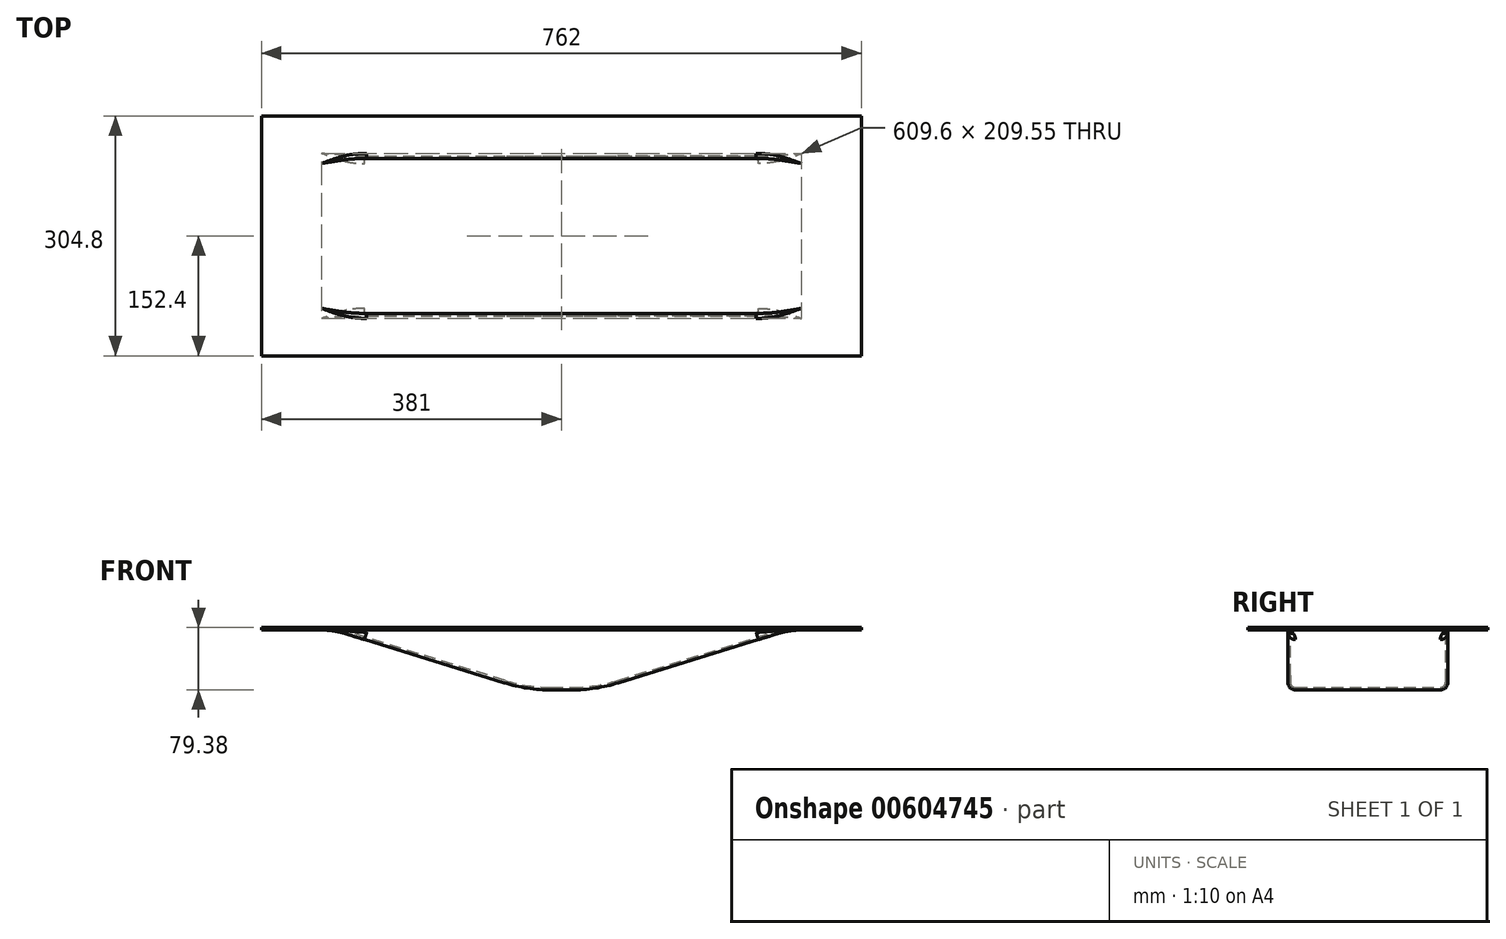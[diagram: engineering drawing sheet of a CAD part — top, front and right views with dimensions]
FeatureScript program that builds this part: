
annotation { "Feature Type Name" : "Feature", "Feature Type Description" : "" }
export const myFeature = defineFeature(function(context is Context, id is Id, definition is map)
    precondition{}
    {
        {
            var Q0;
            Q0=qCreatedBy(makeId("Top.planeOp"),FACE);
            var sketch = newSketch(context, id + "F0", { "sketchPlane" : qUnion([Q0])});
            skLineSegment(sketch, "E0.bottom", {"start": v(-381, 152.4) * mm, "end": v(381, 152.4) * mm});
            skLineSegment(sketch, "E0.top", {"start": v(-381, -152.4) * mm, "end": v(381, -152.4) * mm});
            skLineSegment(sketch, "E0.left", {"start": v(-381, 152.4) * mm, "end": v(-381, -152.4) * mm});
            skLineSegment(sketch, "E0.right", {"start": v(381, 152.4) * mm, "end": v(381, -152.4) * mm});
            skLineSegment(sketch, "E1.bottom", {"start": v(-304.8, 101.6) * mm, "end": v(304.8, 101.6) * mm});
            skLineSegment(sketch, "E1.top", {"start": v(-304.8, -101.6) * mm, "end": v(304.8, -101.6) * mm});
            skLineSegment(sketch, "E1.left", {"start": v(-304.8, 101.6) * mm, "end": v(-304.8, -101.6) * mm});
            skLineSegment(sketch, "E1.right", {"start": v(304.8, 101.6) * mm, "end": v(304.8, -101.6) * mm});
            skLineSegment(sketch, "E2", {"start": v(0, 152.4) * mm, "end": v(0, 101.6) * mm, "construction": true});
            skLineSegment(sketch, "E3", {"start": v(0, 101.6) * mm, "end": v(0, 0) * mm, "construction": true});
            skLineSegment(sketch, "E4", {"start": v(0, 0) * mm, "end": v(304.8, 0) * mm, "construction": true});
            skLineSegment(sketch, "E5", {"start": v(304.8, 0) * mm, "end": v(381, 0) * mm, "construction": true});
            skSolve(sketch);
        }
        {
            var Q0;
            Q0=makeQuery(id+"F0.imprint","IMPRINT",FACE,{"disambiguationData":[TD([[makeQuery(id+"F0.imprint","IMPRINT",EDGE,{"derivedFrom":sQuery(id+"F0.wireOp",EDGE,"E0.bottom")}),-1.0]])]});
            extrude(context, id + "F1", {"entities" : qUnion([Q0]), "oppositeDirection" : true, "depth" : 3.17 * mm});
        }
        {
            var Q0;
            Q0=qCreatedBy(makeId("Front.planeOp"),FACE);
            var sketch = newSketch(context, id + "F2", { "sketchPlane" : qUnion([Q0])});
            skArc(sketch, "E6", {"start": v(-274.8, -4.53) * mm, "mid": v(-289.63, -1.14) * mm, "end": v(-304.8, 0) * mm});
            skLineSegment(sketch, "E7", {"start": v(-274.8, -4.53) * mm, "end": v(-71.76, -67.28) * mm});
            skArc(sketch, "E8", {"start": v(-71.76, -67.28) * mm, "mid": v(-42.57, -73.96) * mm, "end": v(-12.7, -76.2) * mm});
            skLineSegment(sketch, "E9", {"start": v(-12.7, -76.2) * mm, "end": v(0, -76.2) * mm});
            skLineSegment(sketch, "E10", {"start": v(0, -76.2) * mm, "end": v(0, 0) * mm, "construction": true});
            skLineSegment(sketch, "E11.0.MirrorCS", {"start": v(12.7, -76.2) * mm, "end": v(0, -76.2) * mm});
            skArc(sketch, "E12.0.MirrorCS", {"start": v(71.76, -67.28) * mm, "mid": v(42.57, -73.96) * mm, "end": v(12.7, -76.2) * mm});
            skLineSegment(sketch, "E13.0.MirrorCS", {"start": v(274.8, -4.53) * mm, "end": v(71.76, -67.28) * mm});
            skArc(sketch, "E14.0.MirrorCS", {"start": v(274.8, -4.53) * mm, "mid": v(289.63, -1.14) * mm, "end": v(304.8, 0) * mm});
            skLineSegment(sketch, "E15", {"start": v(-275.74, -7.56) * mm, "end": v(-72.7, -70.31) * mm});
            skArc(sketch, "E16", {"start": v(-72.7, -70.31) * mm, "mid": v(-43.04, -77.1) * mm, "end": v(-12.7, -79.38) * mm});
            skLineSegment(sketch, "E17", {"start": v(-12.7, -79.38) * mm, "end": v(0, -79.38) * mm});
            skLineSegment(sketch, "E18.0.MirrorCS", {"start": v(12.7, -79.38) * mm, "end": v(0, -79.38) * mm});
            skArc(sketch, "E19.0.MirrorCS", {"start": v(72.7, -70.31) * mm, "mid": v(43.04, -77.1) * mm, "end": v(12.7, -79.38) * mm});
            skLineSegment(sketch, "E20.0.MirrorCS", {"start": v(275.74, -7.56) * mm, "end": v(72.7, -70.31) * mm});
            skArc(sketch, "E21.0.MirrorCS", {"start": v(275.74, -7.56) * mm, "mid": v(290.1, -4.28) * mm, "end": v(304.8, -3.17) * mm});
            skLineSegment(sketch, "E22", {"start": v(-304.8, 0) * mm, "end": v(-304.8, -3.18) * mm});
            skLineSegment(sketch, "E23.0.MirrorCS", {"start": v(304.8, 0) * mm, "end": v(304.8, -3.18) * mm});
            skArc(sketch, "E24", {"start": v(-275.74, -7.56) * mm, "mid": v(-290.1, -4.28) * mm, "end": v(-304.8, -3.17) * mm});
            skSolve(sketch);
        }
        {
            var Q0;
            Q0=qSketchRegion(id+"F2",true);
            var Q1;
            Q1=makeQuery(id+"F1.opExtrude","SWEPT_FACE",FACE,{"disambiguationData":[OSD([sQuery(id+"F0.wireOp",EDGE,"E1.top")])]});
            extrude(context, id + "F3", {"entities" : qUnion([Q0]), "operationType" : NewBodyOperationType.ADD, "endBound" : BoundingType.SYMMETRIC, "endBoundEntity" : qUnion([Q1]), "depth" : 203.2 * mm});
        }
        {
            var Q0;
            Q0=makeQuery(id+"F1.opExtrude","SWEPT_FACE",FACE,{"disambiguationData":[OSD([sQuery(id+"F0.wireOp",EDGE,"E1.bottom")])]});
            var sketch = newSketch(context, id + "F4", { "sketchPlane" : qUnion([Q0])});
            skLineSegment(sketch, "E25.0", {"start": v(-304.8, 0) * mm, "end": v(304.8, 0) * mm});
            skLineSegment(sketch, "E26.0", {"start": v(-304.8, 0) * mm, "end": v(-304.8, -3.18) * mm});
            skLineSegment(sketch, "E26.2", {"start": v(-275.74, -7.56) * mm, "end": v(-72.7, -70.31) * mm});
            skArc(sketch, "E26.3", {"start": v(-72.7, -70.31) * mm, "mid": v(-43.04, -77.1) * mm, "end": v(-12.7, -79.38) * mm});
            skLineSegment(sketch, "E26.4", {"start": v(-12.7, -79.38) * mm, "end": v(0, -79.38) * mm});
            skLineSegment(sketch, "E26.5", {"start": v(12.7, -79.38) * mm, "end": v(0, -79.38) * mm});
            skArc(sketch, "E26.6", {"start": v(72.7, -70.31) * mm, "mid": v(43.04, -77.1) * mm, "end": v(12.7, -79.38) * mm});
            skLineSegment(sketch, "E26.7", {"start": v(275.74, -7.56) * mm, "end": v(72.7, -70.31) * mm});
            skArc(sketch, "E26.8", {"start": v(275.74, -7.56) * mm, "mid": v(290.1, -4.28) * mm, "end": v(304.8, -3.17) * mm});
            skLineSegment(sketch, "E26.9", {"start": v(304.8, 0) * mm, "end": v(304.8, -3.18) * mm});
            skArc(sketch, "E27.0", {"start": v(-275.74, -7.56) * mm, "mid": v(-290.1, -4.28) * mm, "end": v(-304.8, -3.17) * mm});
            skSolve(sketch);
        }
        {
            var Q0;
            Q0=qSketchRegion(id+"F4",true);
            extrude(context, id + "F5", {"entities" : qUnion([Q0]), "depth" : 3.17 * mm});
        }
        {
            var Q0;
            Q0=makeQuery(id+"F5.opExtrude","SWEPT_BODY",BODY,{"disambiguationData":[OSD([sQuery(id+"F4.wireOp",EDGE,"E25.0"),sQuery(id+"F4.wireOp",EDGE,"E26.0"),sQuery(id+"F4.wireOp",EDGE,"E26.2"),sQuery(id+"F4.wireOp",EDGE,"E26.3"),sQuery(id+"F4.wireOp",EDGE,"E26.4"),sQuery(id+"F4.wireOp",EDGE,"E26.6"),sQuery(id+"F4.wireOp",EDGE,"E26.7"),sQuery(id+"F4.wireOp",EDGE,"E26.8"),sQuery(id+"F4.wireOp",EDGE,"E26.9"),sQuery(id+"F4.wireOp",EDGE,"E27.0")])]});
            var Q1;
            Q1=qCreatedBy(makeId("Front.planeOp"),FACE);
            mirror(context, id + "F6", {"entities" : qUnion([Q0]), "mirrorPlane" : qUnion([Q1])});
        }
        {
            var Q0;
            Q0=makeQuery(id+"F1.opExtrude","SWEPT_BODY",BODY,{"disambiguationData":[OSD([sQuery(id+"F0.wireOp",EDGE,"E0.bottom"),sQuery(id+"F0.wireOp",EDGE,"E0.top"),sQuery(id+"F0.wireOp",EDGE,"E0.left"),sQuery(id+"F0.wireOp",EDGE,"E0.right"),sQuery(id+"F0.wireOp",EDGE,"E1.bottom"),sQuery(id+"F0.wireOp",EDGE,"E1.top"),sQuery(id+"F0.wireOp",EDGE,"E1.left"),sQuery(id+"F0.wireOp",EDGE,"E1.right")])]});
            var Q1;
            Q1=makeQuery(id+"F5.opExtrude","SWEPT_BODY",BODY,{"disambiguationData":[OSD([sQuery(id+"F4.wireOp",EDGE,"E25.0"),sQuery(id+"F4.wireOp",EDGE,"E26.0"),sQuery(id+"F4.wireOp",EDGE,"E26.2"),sQuery(id+"F4.wireOp",EDGE,"E26.3"),sQuery(id+"F4.wireOp",EDGE,"E26.4"),sQuery(id+"F4.wireOp",EDGE,"E26.6"),sQuery(id+"F4.wireOp",EDGE,"E26.7"),sQuery(id+"F4.wireOp",EDGE,"E26.8"),sQuery(id+"F4.wireOp",EDGE,"E26.9"),sQuery(id+"F4.wireOp",EDGE,"E27.0")])]});
            var Q2;
            Q2=makeQuery(id+"F6.opPattern","COPY",BODY,{"derivedFrom":makeQuery(id+"F5.opExtrude","SWEPT_BODY",BODY,{"disambiguationData":[OSD([sQuery(id+"F4.wireOp",EDGE,"E25.0"),sQuery(id+"F4.wireOp",EDGE,"E26.0"),sQuery(id+"F4.wireOp",EDGE,"E26.2"),sQuery(id+"F4.wireOp",EDGE,"E26.3"),sQuery(id+"F4.wireOp",EDGE,"E26.4"),sQuery(id+"F4.wireOp",EDGE,"E26.6"),sQuery(id+"F4.wireOp",EDGE,"E26.7"),sQuery(id+"F4.wireOp",EDGE,"E26.8"),sQuery(id+"F4.wireOp",EDGE,"E26.9"),sQuery(id+"F4.wireOp",EDGE,"E27.0")])]}),"instanceName":"1"});
            booleanBodies(context, id + "F7", {"operationType" : BooleanOperationType.UNION, "tools" : qUnion([Q0, Q1, Q2])});
        }
        {
            var Q0;
            Q0=makeQuery(id+"F7.opBoolean","INTERSECT",EDGE,{"derivedFrom":[makeQuery(id+"F3.opExtrude","SWEPT_FACE",FACE,{"disambiguationData":[OSD([sQuery(id+"F2.wireOp",EDGE,"E7")])]}),makeQuery(id+"F5.opExtrude","CAP_FACE",FACE,{"disambiguationData":[OSD([sQuery(id+"F4.wireOp",EDGE,"E25.0"),sQuery(id+"F4.wireOp",EDGE,"E26.0"),sQuery(id+"F4.wireOp",EDGE,"E26.2"),sQuery(id+"F4.wireOp",EDGE,"E26.3"),sQuery(id+"F4.wireOp",EDGE,"E26.4"),sQuery(id+"F4.wireOp",EDGE,"E26.6"),sQuery(id+"F4.wireOp",EDGE,"E26.7"),sQuery(id+"F4.wireOp",EDGE,"E26.8"),sQuery(id+"F4.wireOp",EDGE,"E26.9"),sQuery(id+"F4.wireOp",EDGE,"E27.0")])],"isStart":false})]});
            var Q1;
            Q1=makeQuery(id+"F7.opBoolean","INTERSECT",EDGE,{"derivedFrom":[makeQuery(id+"F3.opExtrude","SWEPT_FACE",FACE,{"disambiguationData":[OSD([sQuery(id+"F2.wireOp",EDGE,"E7")])]}),makeQuery(id+"F6.opPattern","COPY",FACE,{"derivedFrom":makeQuery(id+"F5.opExtrude","CAP_FACE",FACE,{"disambiguationData":[OSD([sQuery(id+"F4.wireOp",EDGE,"E25.0"),sQuery(id+"F4.wireOp",EDGE,"E26.0"),sQuery(id+"F4.wireOp",EDGE,"E26.2"),sQuery(id+"F4.wireOp",EDGE,"E26.3"),sQuery(id+"F4.wireOp",EDGE,"E26.4"),sQuery(id+"F4.wireOp",EDGE,"E26.6"),sQuery(id+"F4.wireOp",EDGE,"E26.7"),sQuery(id+"F4.wireOp",EDGE,"E26.8"),sQuery(id+"F4.wireOp",EDGE,"E26.9"),sQuery(id+"F4.wireOp",EDGE,"E27.0")])],"isStart":false}),"instanceName":"1"})]});
            var Q2;
            Q2=makeQuery(id+"F5.opExtrude","CAP_EDGE",EDGE,{"disambiguationData":[OSD([sQuery(id+"F4.wireOp",EDGE,"E25.0")])],"isStart":false});
            var Q3;
            Q3=makeQuery(id+"F6.opPattern","COPY",EDGE,{"derivedFrom":makeQuery(id+"F5.opExtrude","CAP_EDGE",EDGE,{"disambiguationData":[OSD([sQuery(id+"F4.wireOp",EDGE,"E25.0")])],"isStart":false}),"instanceName":"1"});
            fillet(context, id + "F8", {"entities" : qUnion([Q0, Q1, Q2, Q3]), "radius" : 6.35 * mm, "tangentPropagation" : true, "allowEdgeOverflow" : false});
        }
        {
            var Q0;
            {var subQ0=sQuery(id+"F0.wireOp",EDGE,"E1.top");var subQ1=makeQuery(id+"F1.opExtrude","CAP_EDGE",EDGE,{"disambiguationData":[OSD([subQ0])],"isStart":false});var subQ2=sQuery(id+"F2.wireOp",EDGE,"E24");var subQ3=sQuery(id+"F2.wireOp",EDGE,"E6");var subQ4=sQuery(id+"F2.wireOp",EDGE,"E14.0.MirrorCS");var subQ5=sQuery(id+"F2.wireOp",EDGE,"E21.0.MirrorCS");var subQ6=makeQuery(id+"F3.opExtrude","CAP_FACE",FACE,{"disambiguationData":[OSD([subQ3,sQuery(id+"F2.wireOp",EDGE,"E7"),sQuery(id+"F2.wireOp",EDGE,"E8"),sQuery(id+"F2.wireOp",EDGE,"E11.0.MirrorCS"),sQuery(id+"F2.wireOp",EDGE,"E12.0.MirrorCS"),sQuery(id+"F2.wireOp",EDGE,"E13.0.MirrorCS"),subQ4,sQuery(id+"F2.wireOp",EDGE,"E15"),sQuery(id+"F2.wireOp",EDGE,"E16"),sQuery(id+"F2.wireOp",EDGE,"E17"),sQuery(id+"F2.wireOp",EDGE,"E19.0.MirrorCS"),sQuery(id+"F2.wireOp",EDGE,"E20.0.MirrorCS"),subQ5,sQuery(id+"F2.wireOp",EDGE,"E22"),sQuery(id+"F2.wireOp",EDGE,"E23.0.MirrorCS"),subQ2])],"isStart":false});var subQ7=makeQuery(id+"F3.opExtrude","SWEPT_FACE",FACE,{"disambiguationData":[OSD([subQ3])]});var subQ8=makeQuery(id+"F1.opExtrude","SWEPT_FACE",FACE,{"disambiguationData":[OSD([subQ0])]});var subQ9=makeQuery(id+"F1.opExtrude","CAP_FACE",FACE,{"disambiguationData":[OSD([sQuery(id+"F0.wireOp",EDGE,"E0.bottom"),sQuery(id+"F0.wireOp",EDGE,"E0.top"),sQuery(id+"F0.wireOp",EDGE,"E0.left"),sQuery(id+"F0.wireOp",EDGE,"E0.right"),sQuery(id+"F0.wireOp",EDGE,"E1.bottom"),subQ0,sQuery(id+"F0.wireOp",EDGE,"E1.left"),sQuery(id+"F0.wireOp",EDGE,"E1.right")])],"isStart":false});var subQ10=makeQuery(id+"F3.opExtrude","SWEPT_FACE",FACE,{"disambiguationData":[OSD([subQ4])]});Q0=makeQuery(id+"F7.opBoolean","MERGE",EDGE,{"derivedFrom":[makeQuery(id+"F3.boolean.opBoolean","SPLIT",EDGE,{"disambiguationData":[TD([subQ9,subQ8,subQ7,subQ6,makeQuery(id+"F3.opExtrude","SWEPT_FACE",FACE,{"disambiguationData":[OSD([subQ2])]})])],"derivedFrom":subQ1}),makeQuery(id+"F3.boolean.opBoolean","SPLIT",EDGE,{"disambiguationData":[TD([subQ9,subQ8,subQ6,subQ10,makeQuery(id+"F3.opExtrude","SWEPT_FACE",FACE,{"disambiguationData":[OSD([subQ5])]})])],"derivedFrom":subQ1}),makeQuery(id+"F3.boolean.opBoolean","SPLIT",EDGE,{"disambiguationData":[TD([subQ9,subQ8,subQ7,subQ6,subQ10])],"derivedFrom":subQ1})]});}
            var Q1;
            {var subQ0=sQuery(id+"F0.wireOp",EDGE,"E1.bottom");var subQ1=makeQuery(id+"F1.opExtrude","CAP_EDGE",EDGE,{"disambiguationData":[OSD([subQ0])],"isStart":false});var subQ2=sQuery(id+"F2.wireOp",EDGE,"E24");var subQ3=sQuery(id+"F2.wireOp",EDGE,"E6");var subQ4=sQuery(id+"F2.wireOp",EDGE,"E14.0.MirrorCS");var subQ5=sQuery(id+"F2.wireOp",EDGE,"E21.0.MirrorCS");var subQ6=makeQuery(id+"F3.opExtrude","CAP_FACE",FACE,{"disambiguationData":[OSD([subQ3,sQuery(id+"F2.wireOp",EDGE,"E7"),sQuery(id+"F2.wireOp",EDGE,"E8"),sQuery(id+"F2.wireOp",EDGE,"E11.0.MirrorCS"),sQuery(id+"F2.wireOp",EDGE,"E12.0.MirrorCS"),sQuery(id+"F2.wireOp",EDGE,"E13.0.MirrorCS"),subQ4,sQuery(id+"F2.wireOp",EDGE,"E15"),sQuery(id+"F2.wireOp",EDGE,"E16"),sQuery(id+"F2.wireOp",EDGE,"E17"),sQuery(id+"F2.wireOp",EDGE,"E19.0.MirrorCS"),sQuery(id+"F2.wireOp",EDGE,"E20.0.MirrorCS"),subQ5,sQuery(id+"F2.wireOp",EDGE,"E22"),sQuery(id+"F2.wireOp",EDGE,"E23.0.MirrorCS"),subQ2])],"isStart":true});var subQ7=makeQuery(id+"F3.opExtrude","SWEPT_FACE",FACE,{"disambiguationData":[OSD([subQ3])]});var subQ8=makeQuery(id+"F1.opExtrude","SWEPT_FACE",FACE,{"disambiguationData":[OSD([subQ0])]});var subQ9=makeQuery(id+"F1.opExtrude","CAP_FACE",FACE,{"disambiguationData":[OSD([sQuery(id+"F0.wireOp",EDGE,"E0.bottom"),sQuery(id+"F0.wireOp",EDGE,"E0.top"),sQuery(id+"F0.wireOp",EDGE,"E0.left"),sQuery(id+"F0.wireOp",EDGE,"E0.right"),subQ0,sQuery(id+"F0.wireOp",EDGE,"E1.top"),sQuery(id+"F0.wireOp",EDGE,"E1.left"),sQuery(id+"F0.wireOp",EDGE,"E1.right")])],"isStart":false});var subQ10=makeQuery(id+"F3.opExtrude","SWEPT_FACE",FACE,{"disambiguationData":[OSD([subQ4])]});Q1=makeQuery(id+"F7.opBoolean","MERGE",EDGE,{"derivedFrom":[makeQuery(id+"F3.boolean.opBoolean","SPLIT",EDGE,{"disambiguationData":[TD([subQ9,subQ8,subQ7,subQ6,makeQuery(id+"F3.opExtrude","SWEPT_FACE",FACE,{"disambiguationData":[OSD([subQ2])]})])],"derivedFrom":subQ1}),makeQuery(id+"F3.boolean.opBoolean","SPLIT",EDGE,{"disambiguationData":[TD([subQ9,subQ8,subQ6,subQ10,makeQuery(id+"F3.opExtrude","SWEPT_FACE",FACE,{"disambiguationData":[OSD([subQ5])]})])],"derivedFrom":subQ1}),makeQuery(id+"F3.boolean.opBoolean","SPLIT",EDGE,{"disambiguationData":[TD([subQ9,subQ8,subQ7,subQ6,subQ10])],"derivedFrom":subQ1})]});}
            fillet(context, id + "F9", {"entities" : qUnion([Q0, Q1]), "radius" : 3.17 * mm, "tangentPropagation" : true, "allowEdgeOverflow" : false});
        }
        {
            var Q0;
            Q0=makeQuery(id+"F3.opExtrude","CAP_EDGE",EDGE,{"disambiguationData":[OSD([sQuery(id+"F2.wireOp",EDGE,"E20.0.MirrorCS")])],"isStart":true});
            var Q1;
            Q1=makeQuery(id+"F3.opExtrude","CAP_EDGE",EDGE,{"disambiguationData":[OSD([sQuery(id+"F2.wireOp",EDGE,"E20.0.MirrorCS")])],"isStart":false});
            fillet(context, id + "F10", {"entities" : qUnion([Q0, Q1]), "radius" : 9.52 * mm, "tangentPropagation" : true, "allowEdgeOverflow" : false});
        }
    });
